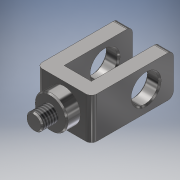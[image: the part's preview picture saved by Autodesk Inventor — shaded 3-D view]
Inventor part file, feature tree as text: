
AUTODESK INVENTOR PART (.ipt)
format: ipt  version: 2018 (Build 220112000, 112)  size: 177,152 bytes
history: native  units: mm
features: extrude x4, sketch x4, other x2, fillet x1, chamfer x1, thread x1
ambient origin geometry x8: Origin, YZ Plane, XZ Plane, XY Plane, X Axis, Y Axis, Z Axis, Center Point
bodies: Solido1 (feature_tree)
feature tree (13):
  extrude  "Estrusione1"  Depth=20.0mm
  extrude  "Estrusione2"  Depth=10.0mm
  fillet  "Raccordo1"  Radius=5.0mm
  extrude  "Estrusione3"  Depth=30.0mm
  extrude  "Estrusione4"  Depth=15.0mm TaperAngle=0.0deg
  chamfer  "Smusso1"  Distance=10.0mm
  thread  "Filettatura2"
  sketch  "Schizzo1"
  sketch  "Schizzo2"
  other  "Linea chiusa proiettata1"
  sketch  "Schizzo3"
  other  "Linea chiusa proiettata2"
  sketch  "Schizzo4"
